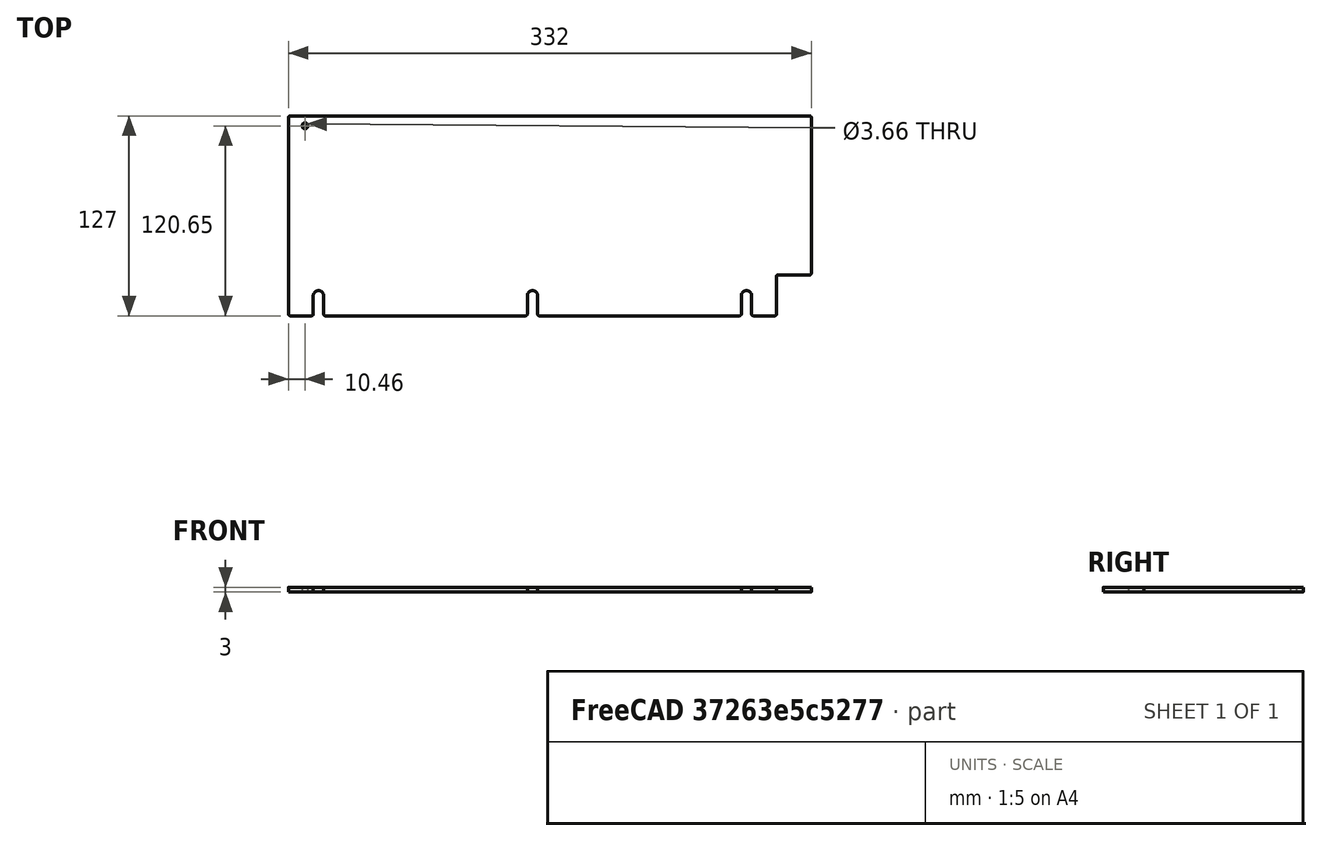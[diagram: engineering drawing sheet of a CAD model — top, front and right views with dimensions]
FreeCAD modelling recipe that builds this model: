
FCSTD DOCUMENT  (FreeCAD 0.21R33675 (Git))
Label: right_wall_back_5in
License: All rights reserved
LicenseURL: http://en.wikipedia.org/wiki/All_rights_reserved
objects: Spreadsheet::Sheet×1, Sketcher::SketchObject×1, PartDesign::Pad×1, PartDesign::Body×1
note: 4 computed .brp shape members not serialized (recipe doc carries the construction recipe); baked Part::Feature solids carry a one-line shape summary decoded from their .brp

FEATURE [Spreadsheet::Sheet] Spreadsheet
  cells = A2='Parameters; A3='Thickness; B3(Thickness)==3 mm; A4='BeamLength; B4(BeamLength)==18 in; A5='BracketLength; B5(BracketLength)==108.6 mm; A6='DistanceLeftBracketEdgeToDoor; B6(DistanceLeftBracketEdgeToDoor)==82.4999 mm; A7='DistanceRightBracketEdgeToDoor; B7(DistanceRightBracketEdgeToDoor)==23.1001 mm; A8='ServoOffsetFromCenter; B8(ServoOffsetFromCenter)==3 in + 1 * (DistanceLeftBracketEdgeToDoor - DistanceRightBracketEdgeToDoor); A9='DoorMargin; B9(DoorMargin)==1 mm; A10='LengthMargin; B10(LengthMargin)==0 mm; A11='LengthLeftBracketEdgeToDoorGap; B11(LengthLeftBracketEdgeToDoorGap)==DistanceLeftBracketEdgeToDoor - DoorMargin; A12='LengthRightBracketEdgeToDoorGap; B12(LengthRightBracketEdgeToDoorGap)==DistanceRightBracketEdgeToDoor - DoorMargin; A13='LengthDoorGap; B13(LengthDoorGap)==BracketLength - LengthLeftBracketEdgeToDoorGap - LengthRightBracketEdgeToDoorGap; A14='BeamLengthMinusBracketLength; B14(BeamLengthMinusBracketLength)==BeamLength - BracketLength; A15='DistanceBackToDoor; B15(DistanceBackToDoor)==0.5 * BeamLengthMinusBracketLength + LengthRightBracketEdgeToDoorGap + ServoOffsetFromCenter; A16='DistanceBackToBracket; B16(DistanceBackToBracket)==0.5 * BeamLengthMinusBracketLength + ServoOffsetFromCenter; A17='LengthBackToDoor; B17(LengthBackToDoor)==DistanceBackToDoor - LengthMargin; A18='LengthBackToBracket; B18(LengthBackToBracket)==DistanceBackToBracket - LengthMargin; A19='Height; B19(Height)==5 in; A21='CutoutMargin; B21(CutoutMargin)==0.5 mm; A22='CutoutHeight; B22(CutoutHeight)==1 in + CutoutMargin; A23='FilletRadius; B23(FilletRadius)==1 mm; A24='MountHoleDiameter; B24(MountHoleDiameter)==0.26 in; A25='MountHoleDistanceFromBottom; B25(MountHoleDistanceFromBottom)==0.5 in; A26='MountHoleSideMargin; B26(MountHoleSideMargin)==0.75 in; A28='RABracketWidth; B28(RABracketWidth)==0.5 in; A29='RABracketHoleDiameter; B29(RABracketHoleDiameter)==0.144 in; A30='RABracketHoleOffset; B30(RABracketHoleOffset)==0.412 in; A31='RAUpperBracketHoleFromTop; B31(RAUpperBracketHoleFromTop)==0.5 * RABracketWidth; A32='RABracketHoleFromSide; B32(RABracketHoleFromSide)==RABracketHoleOffset; B38==3 in + DistanceLeftBracketEdgeToDoor + 0.5 * Thickness - 0.5 * BracketLength
FEATURE [Sketcher::SketchObject] Sketch
  FullyConstrained = true
  MapMode = 5
  Support = -> [XY_Plane]
  expr: Constraints[101] = Spreadsheet.RAUpperBracketHoleFromTop
  expr: Constraints[103] = Spreadsheet.RABracketHoleDiameter
  expr: Constraints[14] = Spreadsheet.FilletRadius
  expr: Constraints[20] = Spreadsheet.Height
  expr: Constraints[43] = Spreadsheet.MountHoleDistanceFromBottom
  expr: Constraints[44] = Spreadsheet.MountHoleDiameter
  expr: Constraints[59] = Spreadsheet.MountHoleSideMargin
  expr: Constraints[7] = Spreadsheet.LengthBackToDoor
  expr: Constraints[8] = Spreadsheet.LengthBackToBracket
  expr: Constraints[9] = Spreadsheet.CutoutHeight
  sketch-geometry (54):
    g0: LineSegment StartX=0 StartY=126 StartZ=0 EndX=0 EndY=1 EndZ=0
    g1: LineSegment StartX=1 StartY=0 StartZ=0 EndX=308.9 EndY=0 EndZ=0
    g2: LineSegment StartX=309.9 StartY=1 StartZ=0 EndX=309.9 EndY=24.9 EndZ=0
    g3: LineSegment StartX=310.9 StartY=25.9 StartZ=0 EndX=331 EndY=25.9 EndZ=0
    g4: LineSegment StartX=332 StartY=26.9 StartZ=0 EndX=332 EndY=126 EndZ=0
    g5: LineSegment StartX=331 StartY=127 StartZ=0 EndX=1 EndY=127 EndZ=0
    g6: ArcOfCircle CenterX=1 CenterY=126 CenterZ=0 NormalX=0 NormalY=0 NormalZ=1 AngleXU=0 Radius=1 StartAngle=1.5708 EndAngle=3.14159
    g7: GeomPoint X=0 Y=127 Z=0
    g8: ArcOfCircle CenterX=1 CenterY=1 CenterZ=0 NormalX=0 NormalY=0 NormalZ=1 AngleXU=0 Radius=1 StartAngle=3.14159 EndAngle=4.71239
    g9: GeomPoint X=0 Y=0 Z=0
    g10: ArcOfCircle CenterX=308.9 CenterY=1 CenterZ=0 NormalX=0 NormalY=0 NormalZ=1 AngleXU=0 Radius=1 StartAngle=4.71239 EndAngle=6.28319
    g11: GeomPoint X=309.9 Y=0 Z=0
    g12: ArcOfCircle CenterX=310.9 CenterY=24.9 CenterZ=0 NormalX=0 NormalY=0 NormalZ=1 AngleXU=0 Radius=1 StartAngle=1.5708 EndAngle=3.14159
    g13: GeomPoint X=309.9 Y=25.9 Z=0
    g14: ArcOfCircle CenterX=331 CenterY=26.9 CenterZ=0 NormalX=0 NormalY=0 NormalZ=1 AngleXU=0 Radius=1 StartAngle=4.71239 EndAngle=6.28319
    g15: GeomPoint X=332 Y=25.9 Z=0
    g16: ArcOfCircle CenterX=331 CenterY=126 CenterZ=0 NormalX=0 NormalY=0 NormalZ=1 AngleXU=0 Radius=1 StartAngle=-2.22e-14 EndAngle=1.5708
    g17: GeomPoint X=332 Y=127 Z=0
    g18: GeomPoint X=19.05 Y=0 Z=0
    g19: LineSegment StartX=19.05 StartY=0 StartZ=0 EndX=19.05 EndY=12.7 EndZ=0
    g20: Circle CenterX=19.05 CenterY=12.7 CenterZ=0 NormalX=0 NormalY=0 NormalZ=1 AngleXU=0 Radius=3.302
    g21: LineSegment StartX=290.85 StartY=12.7 StartZ=0 EndX=290.85 EndY=0 EndZ=0
    g22: LineSegment StartX=290.85 StartY=12.7 StartZ=0 EndX=309.9 EndY=12.7 EndZ=0
    g23: LineSegment StartX=19.05 StartY=12.7 StartZ=0 EndX=0 EndY=12.7 EndZ=0
    g24: Circle CenterX=290.85 CenterY=12.7 CenterZ=0 NormalX=0 NormalY=0 NormalZ=1 AngleXU=0 Radius=3.302
    g25: ArcOfCircle CenterX=19.05 CenterY=12.7 CenterZ=0 NormalX=0 NormalY=0 NormalZ=1 AngleXU=0 Radius=3.302 StartAngle=0 EndAngle=3.14159
    g26: LineSegment StartX=19.05 StartY=12.7 StartZ=0 EndX=22.352 EndY=12.7 EndZ=0
    g27: LineSegment StartX=15.748 StartY=12.7 StartZ=0 EndX=15.748 EndY=1 EndZ=0
    g28: LineSegment StartX=22.352 StartY=12.7 StartZ=0 EndX=22.352 EndY=1 EndZ=0
    g29: ArcOfCircle CenterX=14.748 CenterY=1 CenterZ=0 NormalX=0 NormalY=0 NormalZ=1 AngleXU=0 Radius=1 StartAngle=4.71239 EndAngle=6.28319
    g30: ArcOfCircle CenterX=23.352 CenterY=1 CenterZ=0 NormalX=0 NormalY=0 NormalZ=1 AngleXU=0 Radius=1 StartAngle=3.14159 EndAngle=4.71239
    g31: ArcOfCircle CenterX=290.85 CenterY=12.7 CenterZ=0 NormalX=0 NormalY=0 NormalZ=1 AngleXU=0 Radius=3.302 StartAngle=-3.6e-15 EndAngle=3.14159
    g32: LineSegment StartX=290.85 StartY=12.7 StartZ=0 EndX=287.548 EndY=12.7 EndZ=0
    g33: LineSegment StartX=287.548 StartY=12.7 StartZ=0 EndX=287.548 EndY=1 EndZ=0
    g34: LineSegment StartX=294.152 StartY=12.7 StartZ=0 EndX=294.152 EndY=1 EndZ=0
    g35: ArcOfCircle CenterX=286.548 CenterY=1 CenterZ=0 NormalX=0 NormalY=0 NormalZ=1 AngleXU=0 Radius=1 StartAngle=4.71239 EndAngle=6.28319
    g36: ArcOfCircle CenterX=295.152 CenterY=1 CenterZ=0 NormalX=0 NormalY=0 NormalZ=1 AngleXU=0 Radius=1 StartAngle=3.14159 EndAngle=4.71239
    g37: LineSegment StartX=295.152 StartY=0 StartZ=0 EndX=308.9 EndY=0 EndZ=0
    g38: LineSegment StartX=1 StartY=0 StartZ=0 EndX=14.748 EndY=0 EndZ=0
    g39: LineSegment StartX=0 StartY=127 StartZ=0 EndX=10.46 EndY=127 EndZ=0
    g40: LineSegment StartX=10.46 StartY=127 StartZ=0 EndX=10.46 EndY=120.65 EndZ=0
    g41: Circle CenterX=10.46 CenterY=120.65 CenterZ=0 NormalX=0 NormalY=0 NormalZ=1 AngleXU=0 Radius=1.8288
    g42: GeomPoint X=154.95 Y=0 Z=0
    g43: LineSegment StartX=154.95 StartY=0 StartZ=0 EndX=154.95 EndY=12.7 EndZ=0
    g44: LineSegment StartX=151.648 StartY=12.7 StartZ=0 EndX=158.252 EndY=12.7 EndZ=0
    g45: ArcOfCircle CenterX=154.95 CenterY=12.7 CenterZ=0 NormalX=0 NormalY=0 NormalZ=1 AngleXU=0 Radius=3.302 StartAngle=0 EndAngle=3.14159
    g46: LineSegment StartX=151.648 StartY=12.7 StartZ=0 EndX=151.648 EndY=1 EndZ=0
    g47: LineSegment StartX=158.252 StartY=12.7 StartZ=0 EndX=158.252 EndY=1 EndZ=0
    g48: LineSegment StartX=23.352 StartY=0 StartZ=0 EndX=150.648 EndY=0 EndZ=0
    g49: LineSegment StartX=159.252 StartY=0 StartZ=0 EndX=286.548 EndY=0 EndZ=0
    g50: ArcOfCircle CenterX=150.648 CenterY=1 CenterZ=0 NormalX=0 NormalY=0 NormalZ=1 AngleXU=0 Radius=1 StartAngle=4.71239 EndAngle=6.28319
    g51: GeomPoint X=151.648 Y=0 Z=0
    g52: ArcOfCircle CenterX=159.252 CenterY=1 CenterZ=0 NormalX=0 NormalY=0 NormalZ=1 AngleXU=0 Radius=1 StartAngle=3.14159 EndAngle=4.71239
    g53: GeomPoint X=158.252 Y=0 Z=0
  constraints (130):
    c: Vertical(g0)
    c: Horizontal(g1)
    c: Vertical(g2)
    c: Horizontal(g3)
    c: Vertical(g4)
    c: Horizontal(g5)
    c: Coincident(g-1,g9)
    c: DistanceX(g7,g17) = 332
    c: DistanceX(g9,g11) = 309.9
    c: DistanceY(g11,g13) = 25.9
    c: PointOnObject(g7,g0)
    c: PointOnObject(g7,g5)
    c: Tangent(g0,g6) = -1.5708
    c: Tangent(g5,g6) = -1.5708
    c: Radius(g6) = 1
    c: PointOnObject(g9,g0)
    c: PointOnObject(g9,g1)
    c: Tangent(g0,g8) = -1.5708
    c: Tangent(g1,g8) = -1.5708
    c: Equal(g8,g6)
    c: DistanceY(g1,g5) = 127
    c: PointOnObject(g11,g1)
    c: PointOnObject(g11,g2)
    c: Tangent(g1,g10) = -1.5708
    c: Tangent(g2,g10) = -1.5708
    c: Equal(g10,g8)
    c: PointOnObject(g13,g2)
    c: PointOnObject(g13,g3)
    c: Tangent(g2,g12) = 1.5708
    c: Tangent(g3,g12) = 1.5708
    c: Equal(g12,g10)
    c: PointOnObject(g15,g3)
    c: PointOnObject(g15,g4)
    c: Tangent(g3,g14) = -1.5708
    c: Tangent(g4,g14) = -1.5708
    c: Equal(g14,g12)
    c: PointOnObject(g17,g5)
    c: PointOnObject(g17,g4)
    c: Tangent(g5,g16) = -1.5708
    c: Tangent(g4,g16) = -1.5708
    c: Equal(g16,g14)
    c: Coincident(g19,g18)
    c: Vertical(g19)
    c: DistanceY(g19,g19) = 12.7
    c: Diameter(g20) = 6.604
    c: Coincident(g20,g19)
    c: PointOnObject(g18,g1)
    c: PointOnObject(g21,g1)
    c: Vertical(g21)
    c: Equal(g19,g21)
    c: Coincident(g22,g21)
    c: PointOnObject(g22,g2)
    c: Horizontal(g22)
    c: Coincident(g23,g20)
    c: PointOnObject(g23,g0)
    c: Horizontal(g23)
    c: Equal(g23,g22)
    c: Coincident(g24,g21)
    c: Equal(g24,g20)
    c: DistanceX(g23,g23) = 19.05
    c: Coincident(g25,g19)
    c: PointOnObject(g25,g23)
    c: Coincident(g26,g25)
    c: Coincident(g26,g25)
    c: Horizontal(g26)
    c: PointOnObject(g25,g20)
    c: Coincident(g27,g25)
    c: Vertical(g27)
    c: Coincident(g28,g25)
    c: Vertical(g28)
    c: Equal(g27,g28)
    c: Tangent(g29,g27) = 1.5708
    c: Tangent(g29,g1) = -1.5708
    c: Tangent(g30,g28) = -1.5708
    c: Tangent(g30,g1) = -1.5708
    c: Equal(g29,g8)
    c: Coincident(g31,g21)
    c: PointOnObject(g31,g22)
    c: Coincident(g32,g31)
    c: Coincident(g32,g31)
    c: Horizontal(g32)
    c: PointOnObject(g31,g24)
    c: Coincident(g33,g31)
    c: Vertical(g33)
    c: Coincident(g34,g31)
    c: Vertical(g34)
    c: Equal(g33,g34)
    c: Tangent(g35,g33) = 1.5708
    c: Tangent(g35,g1) = -1.5708
    c: Tangent(g36,g34) = -1.5708
    c: Tangent(g36,g1) = -1.5708
    c: Equal(g36,g10)
    c: Coincident(g37,g36)
    c: Coincident(g37,g10)
    c: Coincident(g38,g8)
    c: Coincident(g38,g29)
    c: Horizontal(g39)
    c: Coincident(g7,g39)
    c: DistanceX(g39,g39) = 10.46
    c: Coincident(g40,g39)
    c: Vertical(g40)
    c: DistanceY(g40,g40) = 6.35
    c: Coincident(g41,g40)
    c: Diameter(g41) = 3.6576
    c: Symmetric(g30,g35,g42)
    c: Coincident(g43,g42)
    c: Vertical(g43)
    c: Symmetric(g44,g44,g43)
    c: Coincident(g45,g44)
    c: Coincident(g45,g44)
    c: Horizontal(g44)
    c: Vertical(g46)
    c: Tangent(g46,g45) = -1.5708
    c: Tangent(g47,g45) = 1.5708
    c: PointOnObject(g51,g1)
    c: PointOnObject(g53,g1)
    c: Coincident(g48,g30)
    c: Coincident(g49,g35)
    c: Equal(g21,g43)
    c: Equal(g25,g45)
    c: PointOnObject(g51,g46)
    c: PointOnObject(g51,g48)
    c: Tangent(g46,g50) = 1.5708
    c: Tangent(g48,g50) = -1.5708
    c: PointOnObject(g53,g47)
    c: PointOnObject(g53,g49)
    c: Tangent(g47,g52) = -1.5708
    c: Tangent(g49,g52) = -1.5708
    c: Equal(g50,g30)
    c: Equal(g52,g35)
FEATURE [PartDesign::Pad] Pad
  Direction = (0,0,1)
  Length = 3
  Length2 = 10
  Profile = -> Sketch
  ReferenceAxis = -> Sketch [N_Axis]
  Type = 0
  expr: Length = Spreadsheet.Thickness
FEATURE [PartDesign::Body] Body
  Group = -> [Sketch,Pad]
  Origin = -> Origin
  Tip = -> Pad
